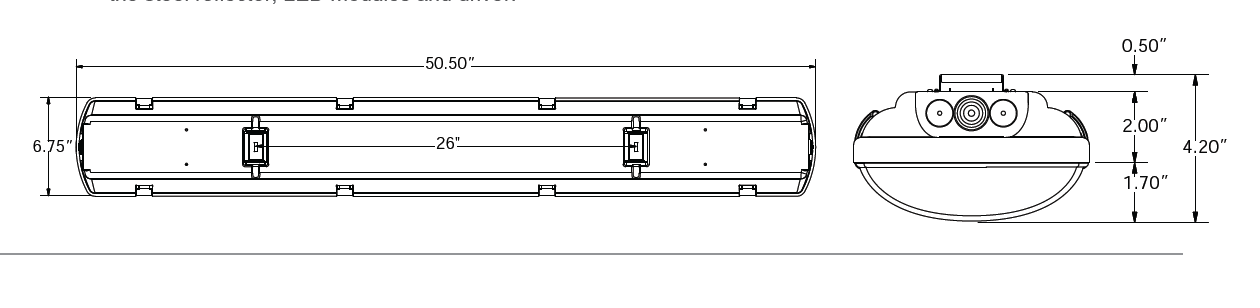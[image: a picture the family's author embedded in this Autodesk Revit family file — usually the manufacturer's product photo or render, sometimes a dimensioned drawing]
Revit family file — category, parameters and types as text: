
# Revit family: BS100LEDX4
name_source: partatom
category: Lighting Fixtures
revit_build: Autodesk Revit LT 2017 (Build: 20160225_1515(x64)
units: mm (PartAtom-declared; Revit-internal decimal feet)

## family parameters
Cut with Voids When Loaded = No
Host = Face
Light Source = Yes
Part Type = Normal
Room Calculation Point = No
Round Connector Dimension = Use Diameter
Shared = No

## types (2) — shared parameters
Color Filter = 16777215
Default Elevation = 4' - 0"
Description = The ILLUMINA® BS100LED is ideal for various applications
including retail, industrial, parking garages, carport, parking structures,
warehouses, breezeways, canopies, schools and much more. It can be
installed both indoor and outdoor.
Dimming Lamp Color Temperature Shift = <None>
Emit from Line Length = 2' - 0"
Keynote = ILLUMINA FAMILY
Lamp = LED
Manufacturer = BEGHELLI NORTH AMERICA
Model = BS100LEDX4
Tilt Angle = -90.00°
Type Image = BS100LED IMAGE.PNG
Wattage Comments = 100W

## per-type parameters (varying)
| type | Photometric Web File |
| BS100LEDX4-HTHOWT40 | BS100LEDX4HTHOWT40120V-277V TO REVIT.ies |
| BS100LEDX4-HTLOWT40 | BS100LEDX4HTLOWT40120V-277V TO REVIT.ies |

## geometry (parser evidence)
native form markers: Sweep x46
no freeform markers — native parametric forms only
